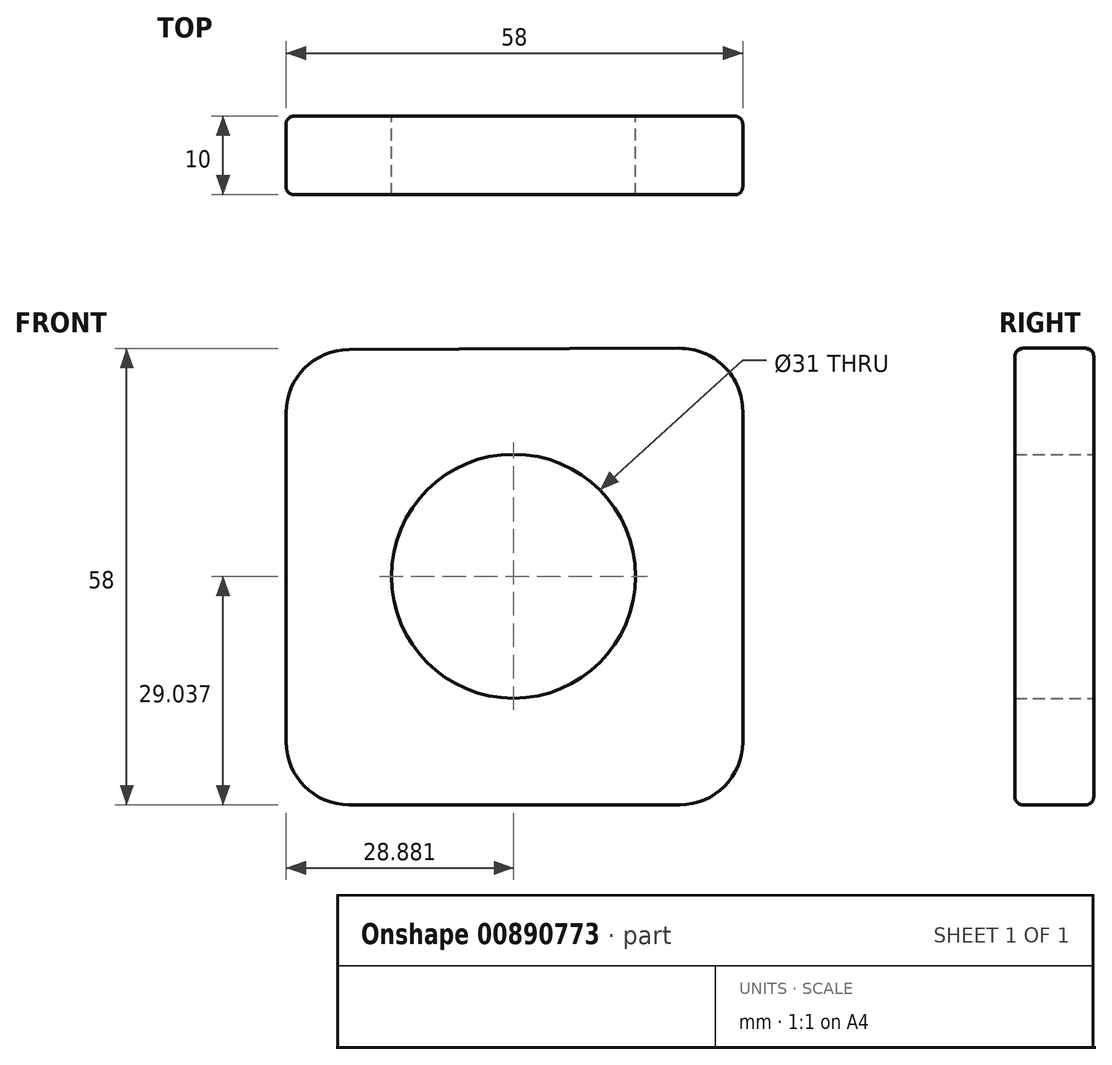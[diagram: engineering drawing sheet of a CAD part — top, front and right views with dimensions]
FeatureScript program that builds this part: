
annotation { "Feature Type Name" : "Feature", "Feature Type Description" : "" }
export const myFeature = defineFeature(function(context is Context, id is Id, definition is map)
    precondition{}
    {
        {
            var Q0;
            Q0=qCreatedBy(makeId("Front.planeOp"),FACE);
            var sketch = newSketch(context, id + "F0", { "sketchPlane" : qUnion([Q0])});
            skLineSegment(sketch, "E0", {"start": v(-90.9, 19.34) * mm, "end": v(-90.9, -22.49) * mm});
            skLineSegment(sketch, "E1", {"start": v(-82.9, -30.49) * mm, "end": v(-40.9, -30.49) * mm});
            skLineSegment(sketch, "E2", {"start": v(-32.9, -22.49) * mm, "end": v(-32.9, 19.51) * mm});
            skLineSegment(sketch, "E3", {"start": v(-40.93, 27.51) * mm, "end": v(-82.93, 27.34) * mm});
            skPoint(sketch, "E4.visualSharp", {"position": v(-90.9, 27.3) * mm});
            skArc(sketch, "E4.filletArc", {"start": v(-82.93, 27.34) * mm, "mid": v(-88.57, 24.98) * mm, "end": v(-90.9, 19.34) * mm});
            skPoint(sketch, "E5.visualSharp", {"position": v(-32.9, 27.55) * mm});
            skArc(sketch, "E5.filletArc", {"start": v(-32.9, 19.51) * mm, "mid": v(-35.25, 25.18) * mm, "end": v(-40.93, 27.51) * mm});
            skPoint(sketch, "E6.visualSharp", {"position": v(-32.9, -30.49) * mm});
            skArc(sketch, "E6.filletArc", {"start": v(-40.9, -30.49) * mm, "mid": v(-35.24, -28.14) * mm, "end": v(-32.9, -22.49) * mm});
            skPoint(sketch, "E7.visualSharp", {"position": v(-90.9, -30.49) * mm});
            skArc(sketch, "E7.filletArc", {"start": v(-90.9, -22.49) * mm, "mid": v(-88.55, -28.14) * mm, "end": v(-82.9, -30.49) * mm});
            skCircle(sketch, "E8", {"center": v(-62.02, -1.45) * mm, "radius": 15.5 * mm});
            skSolve(sketch);
        }
        {
            var Q0;
            Q0=makeQuery(id+"F0.imprint","IMPRINT",FACE,{"disambiguationData":[TD([[makeQuery(id+"F0.imprint","IMPRINT",EDGE,{"derivedFrom":sQuery(id+"F0.wireOp",EDGE,"E0")}),1.0]])]});
            extrude(context, id + "F1", {"entities" : qUnion([Q0]), "depth" : 10 * mm, "offsetDistance" : 25.4 * mm});
        }
        {
            var Q0;
            Q0=makeQuery(id+"F1.opExtrude","CAP_EDGE",EDGE,{"disambiguationData":[OSD([sQuery(id+"F0.wireOp",EDGE,"E7.filletArc")])],"isStart":false});
            var Q1;
            Q1=makeQuery(id+"F1.opExtrude","CAP_EDGE",EDGE,{"disambiguationData":[OSD([sQuery(id+"F0.wireOp",EDGE,"E6.filletArc")])],"isStart":true});
            var Q2;
            Q2=makeQuery(id+"F1.opExtrude","CAP_EDGE",EDGE,{"disambiguationData":[OSD([sQuery(id+"F0.wireOp",EDGE,"E1")])],"isStart":true});
            var Q3;
            Q3=makeQuery(id+"F1.opExtrude","CAP_EDGE",EDGE,{"disambiguationData":[OSD([sQuery(id+"F0.wireOp",EDGE,"E0")])],"isStart":true});
            var Q4;
            Q4=makeQuery(id+"F1.opExtrude","CAP_EDGE",EDGE,{"disambiguationData":[OSD([sQuery(id+"F0.wireOp",EDGE,"E7.filletArc")])],"isStart":true});
            fillet(context, id + "F2", {"entities" : qUnion([Q0, Q1, Q2, Q3, Q4]), "radius" : 1 * mm, "tangentPropagation" : true, "allowEdgeOverflow" : false});
        }
    });
